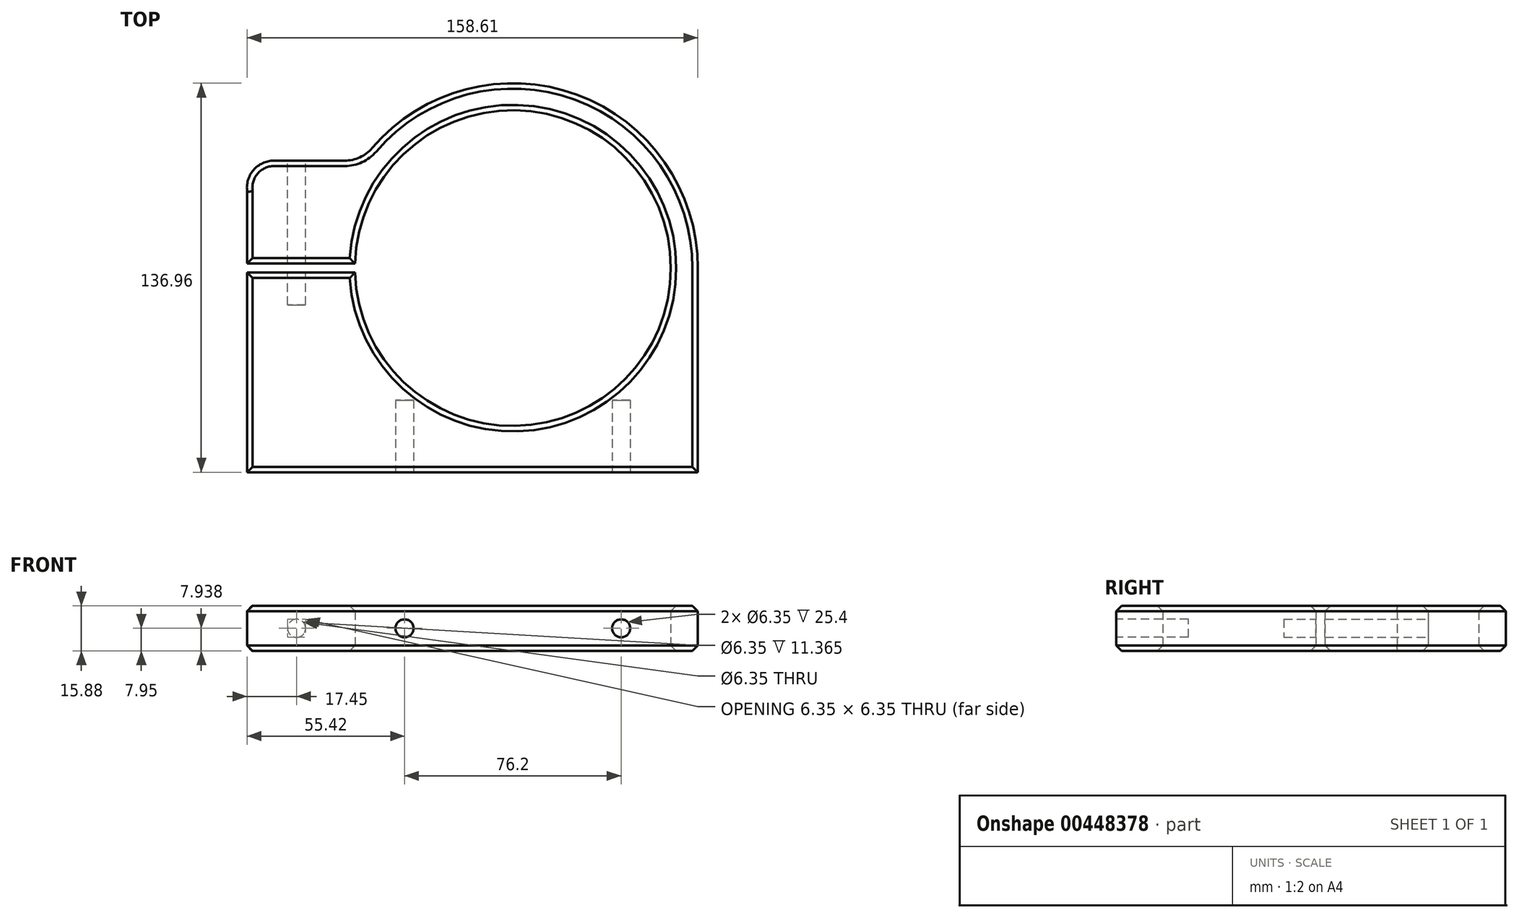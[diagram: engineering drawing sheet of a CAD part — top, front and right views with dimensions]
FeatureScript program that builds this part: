
annotation { "Feature Type Name" : "Feature", "Feature Type Description" : "" }
export const myFeature = defineFeature(function(context is Context, id is Id, definition is map)
    precondition{}
    {
        {
            var Q0;
            Q0=qCreatedBy(makeId("Top.planeOp"),FACE);
            var sketch = newSketch(context, id + "F0", { "sketchPlane" : qUnion([Q0])});
            skArc(sketch, "E0", {"start": v(-55.54, -1.6) * mm, "mid": v(55.56, 0.01) * mm, "end": v(-55.54, 1.57) * mm});
            skArc(sketch, "E1.0", {"start": v(65.09, 0) * mm, "mid": v(22.54, 61.06) * mm, "end": v(-49.48, 42.28) * mm});
            skArc(sketch, "E2", {"start": v(-84, 37.84) * mm, "mid": v(-91.21, 34.52) * mm, "end": v(-93.41, 26.9) * mm});
            skLineSegment(sketch, "E3.top", {"start": v(-93.41, -71.87) * mm, "end": v(65.09, -71.87) * mm});
            skLineSegment(sketch, "E3.left", {"start": v(-93.41, 29.73) * mm, "end": v(-93.41, 1.57) * mm});
            skLineSegment(sketch, "E3.right", {"start": v(65.09, 0) * mm, "end": v(65.09, -71.87) * mm});
            skLineSegment(sketch, "E4", {"start": v(-84, 37.84) * mm, "end": v(-59.14, 37.84) * mm});
            skPoint(sketch, "E5.visualSharp", {"position": v(-52.96, 37.84) * mm});
            skArc(sketch, "E5.filletArc", {"start": v(-59.14, 37.84) * mm, "mid": v(-53.82, 39) * mm, "end": v(-49.48, 42.28) * mm});
            skLineSegment(sketch, "E6", {"start": v(-55.54, 1.57) * mm, "end": v(-93.41, 1.57) * mm});
            skLineSegment(sketch, "E7", {"start": v(-55.54, -1.6) * mm, "end": v(-93.41, -1.6) * mm});
            skPoint(sketch, "E8.orphan", {"position": v(0, -1.6) * mm});
            skPoint(sketch, "E9.orphan", {"position": v(0, 1.57) * mm});
            skLineSegment(sketch, "E10.trimOffspring", {"start": v(-93.41, -1.6) * mm, "end": v(-93.41, -71.87) * mm});
            skSolve(sketch);
        }
        {
            var Q0;
            Q0 = qSketchRegion(id + "F0", true);
            extrude(context, id + "F1", {"entities" : qUnion([Q0]), "depth" : 15.88 * mm});
        }
        {
            var Q0;
            Q0=makeQuery(id+"F1.opExtrude","SWEPT_FACE",FACE,{"disambiguationData":[OSD([sQuery(id+"F0.wireOp",EDGE,"E4")])]});
            var sketch = newSketch(context, id + "F2", { "sketchPlane" : qUnion([Q0])});
            skCircle(sketch, "E11", {"center": v(76.07, 7.95) * mm, "radius": 3.18 * mm});
            skSolve(sketch);
        }
        {
            var Q0;
            Q0 = qSketchRegion(id + "F2", true);
            extrude(context, id + "F3", {"entities" : qUnion([Q0]), "operationType" : NewBodyOperationType.REMOVE, "oppositeDirection" : true, "depth" : 50.8 * mm});
        }
        {
            var Q0;
            Q0=makeQuery(id+"F1.opExtrude","SWEPT_FACE",FACE,{"disambiguationData":[OSD([sQuery(id+"F0.wireOp",EDGE,"E3.top")])]});
            var sketch = newSketch(context, id + "F4", { "sketchPlane" : qUnion([Q0])});
            skCircle(sketch, "E12", {"center": v(-38.1, 7.94) * mm, "radius": 3.18 * mm});
            skCircle(sketch, "E13", {"center": v(38.1, 7.94) * mm, "radius": 3.18 * mm});
            skSolve(sketch);
        }
        {
            var Q0;
            Q0 = qSketchRegion(id + "F4", true);
            extrude(context, id + "F5", {"entities" : qUnion([Q0]), "operationType" : NewBodyOperationType.REMOVE, "oppositeDirection" : true, "depth" : 25.4 * mm});
        }
        {
            var Q0;
            Q0=makeQuery(id+"F1.opExtrude","CAP_FACE",FACE,{"disambiguationData":[OSD([sQuery(id+"F0.wireOp",EDGE,"E0"),sQuery(id+"F0.wireOp",EDGE,"E1.0"),sQuery(id+"F0.wireOp",EDGE,"E2"),sQuery(id+"F0.wireOp",EDGE,"E3.top"),sQuery(id+"F0.wireOp",EDGE,"E3.left"),sQuery(id+"F0.wireOp",EDGE,"E3.right"),sQuery(id+"F0.wireOp",EDGE,"E4"),sQuery(id+"F0.wireOp",EDGE,"E5.filletArc"),sQuery(id+"F0.wireOp",EDGE,"E6"),sQuery(id+"F0.wireOp",EDGE,"E7"),sQuery(id+"F0.wireOp",EDGE,"E10.trimOffspring")])],"isStart":false});
            var Q1;
            Q1=makeQuery(id+"F1.opExtrude","CAP_FACE",FACE,{"disambiguationData":[OSD([sQuery(id+"F0.wireOp",EDGE,"E0"),sQuery(id+"F0.wireOp",EDGE,"E1.0"),sQuery(id+"F0.wireOp",EDGE,"E2"),sQuery(id+"F0.wireOp",EDGE,"E3.top"),sQuery(id+"F0.wireOp",EDGE,"E3.left"),sQuery(id+"F0.wireOp",EDGE,"E3.right"),sQuery(id+"F0.wireOp",EDGE,"E4"),sQuery(id+"F0.wireOp",EDGE,"E5.filletArc"),sQuery(id+"F0.wireOp",EDGE,"E6"),sQuery(id+"F0.wireOp",EDGE,"E7"),sQuery(id+"F0.wireOp",EDGE,"E10.trimOffspring")])],"isStart":true});
            chamfer(context, id + "F6", {"entities" : qUnion([Q0, Q1]), "width" : 1.9 * mm, "tangentPropagation" : true});
        }
    });
